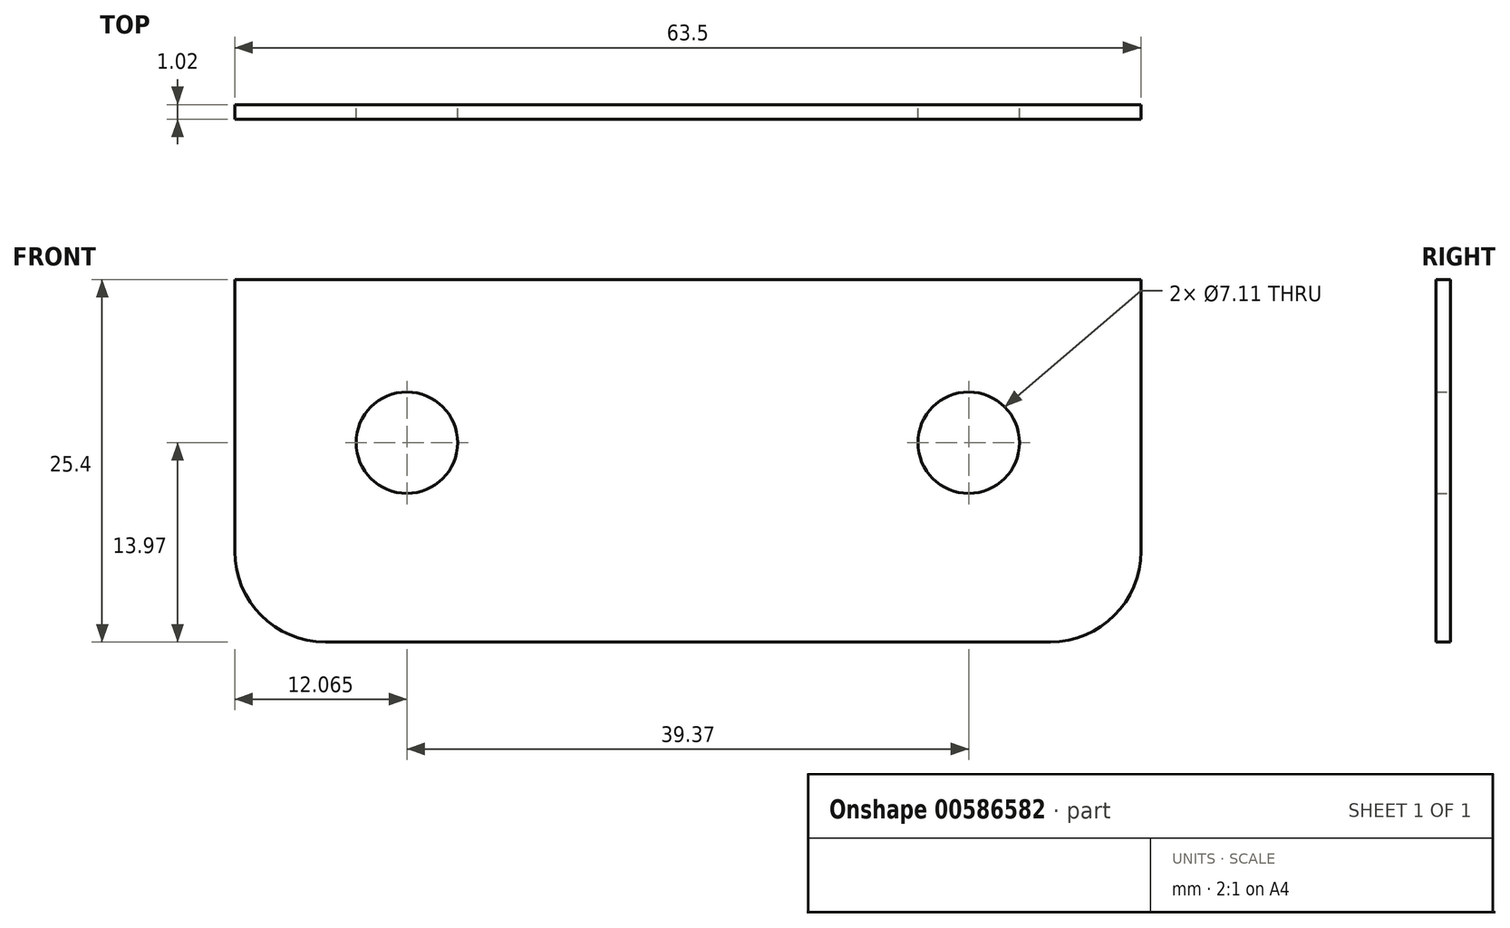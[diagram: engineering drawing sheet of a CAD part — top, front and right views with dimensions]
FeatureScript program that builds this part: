
annotation { "Feature Type Name" : "Feature", "Feature Type Description" : "" }
export const myFeature = defineFeature(function(context is Context, id is Id, definition is map)
    precondition{}
    {
        {
            var Q0;
            Q0=qCreatedBy(makeId("Front.planeOp"),FACE);
            var sketch = newSketch(context, id + "F0", { "sketchPlane" : qUnion([Q0])});
            skLineSegment(sketch, "E0.bottom", {"start": v(31.75, 12.7) * mm, "end": v(-31.75, 12.7) * mm});
            skLineSegment(sketch, "E0.top", {"start": v(25.4, -12.7) * mm, "end": v(-25.4, -12.7) * mm});
            skLineSegment(sketch, "E0.left", {"start": v(31.75, 12.7) * mm, "end": v(31.75, -6.35) * mm});
            skLineSegment(sketch, "E0.right", {"start": v(-31.75, 12.7) * mm, "end": v(-31.75, -6.35) * mm});
            skPoint(sketch, "E0.middle", {"position": v(0, 0) * mm});
            skPoint(sketch, "E1.visualSharp", {"position": v(-31.75, -12.7) * mm});
            skArc(sketch, "E1.filletArc", {"start": v(-31.75, -6.35) * mm, "mid": v(-29.9, -10.84) * mm, "end": v(-25.4, -12.7) * mm});
            skPoint(sketch, "E2.visualSharp", {"position": v(31.75, -12.7) * mm});
            skArc(sketch, "E2.filletArc", {"start": v(25.4, -12.7) * mm, "mid": v(29.9, -10.84) * mm, "end": v(31.75, -6.35) * mm});
            skCircle(sketch, "E3", {"center": v(-19.69, 1.27) * mm, "radius": 3.56 * mm});
            skCircle(sketch, "E4", {"center": v(19.69, 1.27) * mm, "radius": 3.56 * mm});
            skSolve(sketch);
        }
        {
            var Q0;
            Q0=makeQuery(id+"F0.imprint","IMPRINT",FACE,{"disambiguationData":[TD([[makeQuery(id+"F0.imprint","IMPRINT",EDGE,{"derivedFrom":sQuery(id+"F0.wireOp",EDGE,"E0.bottom")}),1.0]])]});
            extrude(context, id + "F1", {"entities" : qUnion([Q0]), "depth" : 1.02 * mm, "offsetDistance" : 25.4 * mm});
        }
    });
